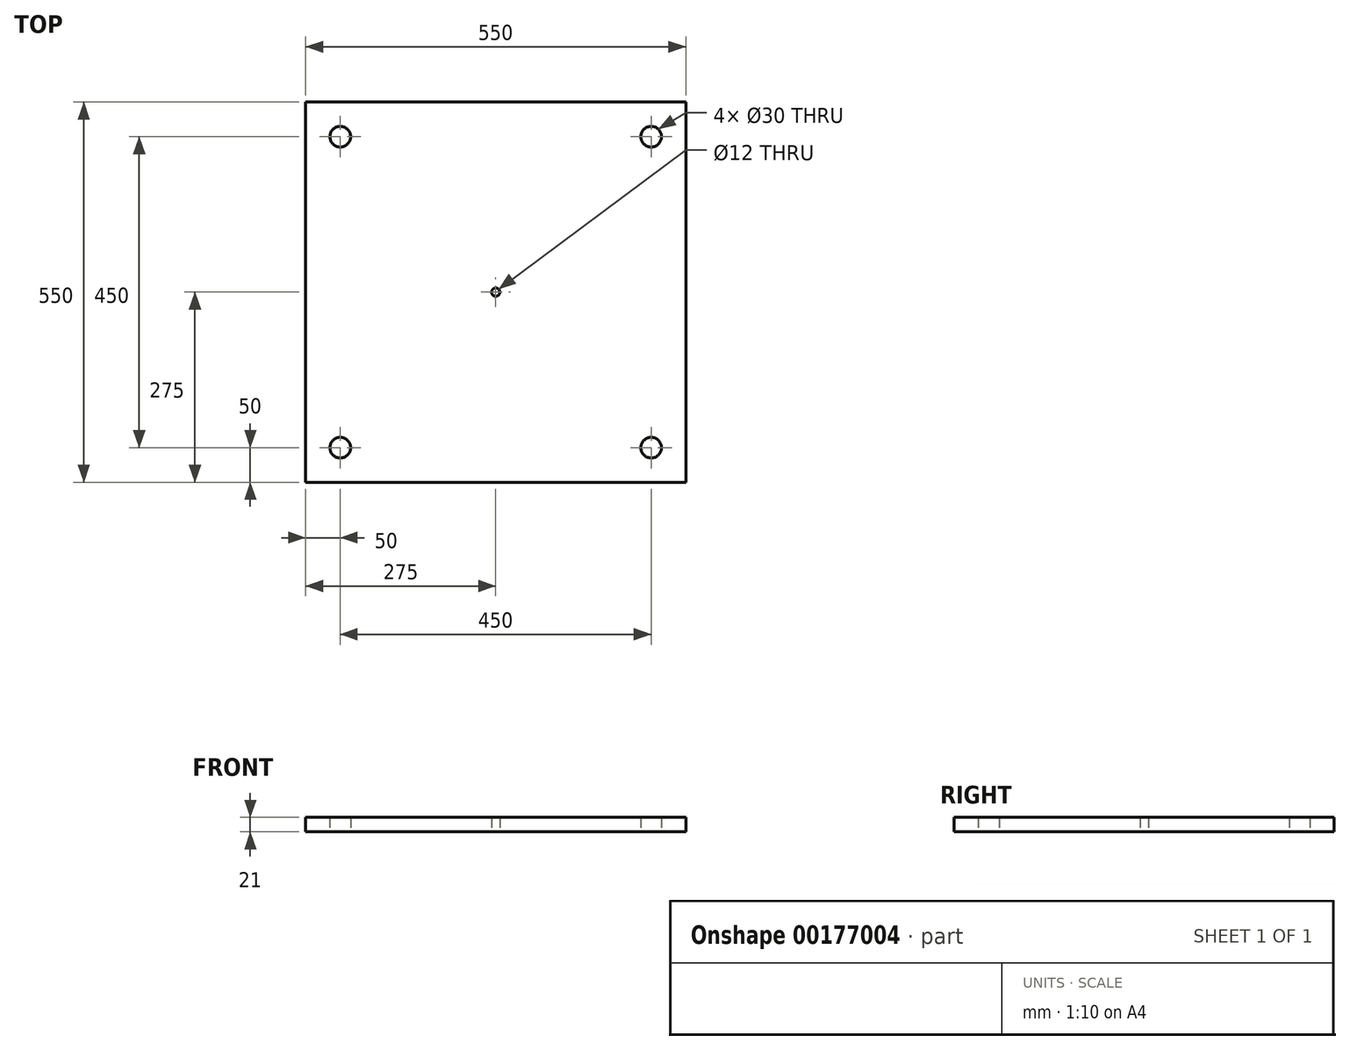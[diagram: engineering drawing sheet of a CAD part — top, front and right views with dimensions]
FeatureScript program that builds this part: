
annotation { "Feature Type Name" : "Feature", "Feature Type Description" : "" }
export const myFeature = defineFeature(function(context is Context, id is Id, definition is map)
    precondition{}
    {
        {
            var Q0;
            Q0=qCreatedBy(makeId("Top.planeOp"),FACE);
            var sketch = newSketch(context, id + "F0", { "sketchPlane" : qUnion([Q0])});
            skLineSegment(sketch, "E0.bottom", {"start": v(275, 275) * mm, "end": v(-275, 275) * mm});
            skLineSegment(sketch, "E0.top", {"start": v(275, -275) * mm, "end": v(-275, -275) * mm});
            skLineSegment(sketch, "E0.left", {"start": v(275, 275) * mm, "end": v(275, -275) * mm});
            skLineSegment(sketch, "E0.right", {"start": v(-275, 275) * mm, "end": v(-275, -275) * mm});
            skPoint(sketch, "E0.middle", {"position": v(0, 0) * mm});
            skCircle(sketch, "E1", {"center": v(0, 0) * mm, "radius": 6 * mm});
            skLineSegment(sketch, "E2", {"start": v(-313.58, 225) * mm, "end": v(369.96, 225) * mm, "construction": true});
            skLineSegment(sketch, "E3", {"start": v(-351.77, -225) * mm, "end": v(364.39, -225) * mm, "construction": true});
            skLineSegment(sketch, "E4", {"start": v(-225, 298.2) * mm, "end": v(-225, -286.7) * mm, "construction": true});
            skLineSegment(sketch, "E5", {"start": v(225, 295.9) * mm, "end": v(225, -300.5) * mm, "construction": true});
            skCircle(sketch, "E6", {"center": v(-225, 225) * mm, "radius": 15 * mm});
            skCircle(sketch, "E7", {"center": v(225, 225) * mm, "radius": 15 * mm});
            skCircle(sketch, "E8", {"center": v(225, -225) * mm, "radius": 15 * mm});
            skCircle(sketch, "E9", {"center": v(-225, -225) * mm, "radius": 15 * mm});
            skSolve(sketch);
        }
        {
            var Q0;
            Q0=makeQuery(id+"F0.imprint","IMPRINT",FACE,{"disambiguationData":[TD([[makeQuery(id+"F0.imprint","IMPRINT",EDGE,{"derivedFrom":sQuery(id+"F0.wireOp",EDGE,"E0.bottom")}),1.0]])]});
            extrude(context, id + "F1", {"entities" : qUnion([Q0]), "depth" : 21 * mm});
        }
    });
